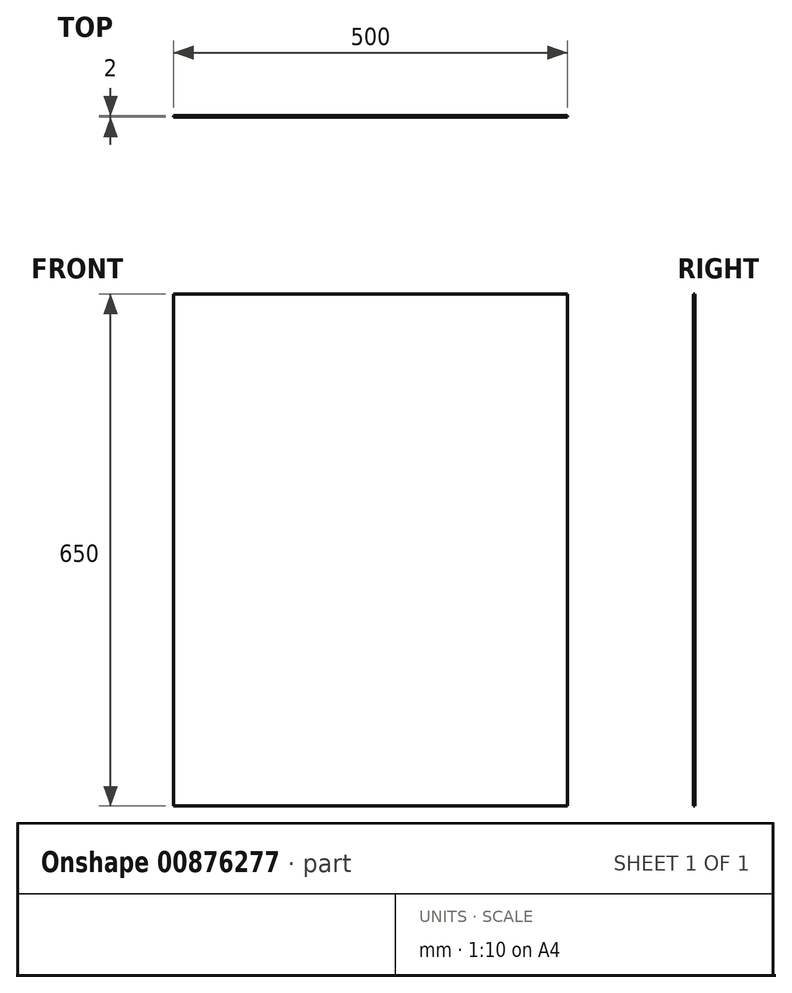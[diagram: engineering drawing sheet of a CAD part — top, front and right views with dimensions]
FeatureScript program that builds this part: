
annotation { "Feature Type Name" : "Feature", "Feature Type Description" : "" }
export const myFeature = defineFeature(function(context is Context, id is Id, definition is map)
    precondition{}
    {
        {
            var Q0;
            Q0=qCreatedBy(makeId("Front.planeOp"),FACE);
            var sketch = newSketch(context, id + "F0", { "sketchPlane" : qUnion([Q0])});
            skLineSegment(sketch, "E0.bottom", {"start": v(250, 325) * mm, "end": v(-250, 325) * mm});
            skLineSegment(sketch, "E0.top", {"start": v(250, -325) * mm, "end": v(-250, -325) * mm});
            skLineSegment(sketch, "E0.left", {"start": v(250, 325) * mm, "end": v(250, -325) * mm});
            skLineSegment(sketch, "E0.right", {"start": v(-250, 325) * mm, "end": v(-250, -325) * mm});
            skPoint(sketch, "E0.middle", {"position": v(0, 0) * mm});
            skSolve(sketch);
        }
        {
            var Q0;
            Q0=makeQuery(id+"F0.imprint","IMPRINT",FACE,{"disambiguationData":[TD([[makeQuery(id+"F0.imprint","IMPRINT",EDGE,{"derivedFrom":sQuery(id+"F0.wireOp",EDGE,"E0.bottom")}),1.0]])]});
            extrude(context, id + "F1", {"entities" : qUnion([Q0]), "depth" : 2 * mm, "offsetDistance" : 25.4 * mm});
        }
    });
